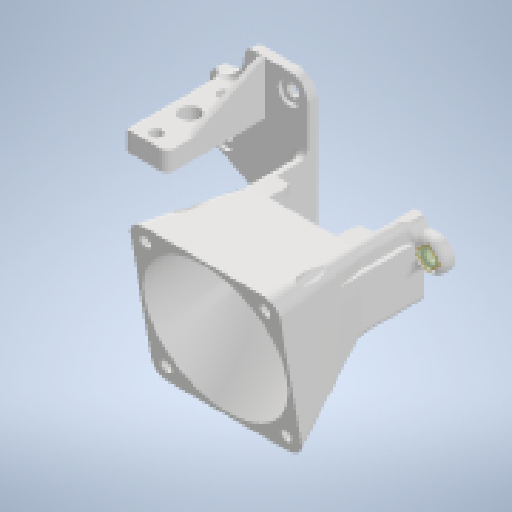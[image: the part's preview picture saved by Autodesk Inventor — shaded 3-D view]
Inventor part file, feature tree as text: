
AUTODESK INVENTOR PART (.ipt)
format: ipt  version: 2023 (Build 270158000, 158)  size: 935,936 bytes
history: native  units: mm
features: extrude x19, sketch x19, reference x19, other x11, fillet x10, plane x7, loft x2, projected_geometry x2
ambient origin geometry x8: Origin, YZ Plane, XZ Plane, XY Plane, X Axis, Y Axis, Z Axis, Center Point
bodies: Solid1 (feature_tree)
feature tree (89):
  extrude  "Extrusion1"  Depth=2.5mm TaperAngle=0.0deg
  extrude  "Extrusion2"  Depth=1.0mm TaperAngle=0.0deg
  extrude  "Extrusion3"  Depth=12.0mm TaperAngle=0.0deg
  extrude  "Extrusion4"  Depth=14.45mm TaperAngle=0.0deg
  extrude  "Extrusion6"  TaperAngle=90.0deg  [1 undecoded]
  extrude  "Extrusion7"  Depth=6.0mm
  extrude  "Extrusion8"  Depth=19.0mm
  plane  "Work Plane2"
  fillet  "Fillet1"  Radius=2.0mm
  fillet  "Fillet2"  Radius=2.0mm
  fillet  "Fillet3"  Radius=2.5mm
  extrude  "Extrusion9"  Depth=2.0mm
  fillet  "Fillet4"  Radius=38.0mm
  plane  "Work Plane4"
  sketch  "Sketch12"  dims[d38=20.0mm d40=12.217305mm]
  loft  "Loft2"
  loft  "Loft3"
  fillet  "Fillet5"  Radius=40.0mm
  extrude  "Extrusion10"  Depth=4.0mm
  fillet  "Fillet6"  Radius=2.8mm
  fillet  "Fillet7"  Radius=38.0mm
  extrude  "Extrusion11"  Depth=20.0mm
  fillet  "Fillet8"  [1 undecoded]
  extrude  "Extrusion12"  TaperAngle=0.0deg  [1 undecoded]
  plane  "Work Plane5"
  extrude  "Extrusion13"  Depth=2.0mm
  plane  "Work Plane7"
  extrude  "Extrusion16"  Depth=3.5mm
  fillet  "Fillet9"  Radius=2.5mm
  extrude  "Extrusion17"  Depth=100.0mm TaperAngle=0.0deg
  extrude  "Extrusion18"  Depth=19.5mm
  extrude  "Extrusion19"  Depth=3.0mm
  extrude  "Extrusion20"  Depth=3.75mm
  fillet  "Fillet10"  Radius=4.75mm
  extrude  "Extrusion21"  Depth=4.75mm
  plane  "Work Plane8"
  extrude  "Extrusion22"  Depth=10.0mm
  sketch  "Sketch1"  dims[d1=2.5mm d2=2.5mm d3=0.0mm]
  reference  "Reference1"
  reference  "Reference2"
  sketch  "Sketch2"  dims[d4=6.0mm d5=1.0mm d6=0.0mm]
  sketch  "Sketch3"  dims[d7=2.0mm d8=12.0mm d9=0.0mm]
  sketch  "Sketch4"  dims[d11=3.0mm d12=0.0mm d17=14.45mm d18=0.0mm]
  sketch  "Sketch6"  dims[d19=90.0deg d21=90.0deg]
  sketch  "Sketch7"  dims[d22=3.5mm d23=0.0mm d24=6.0mm]
  reference  "Reference10"
  reference  "Reference11"
  sketch  "Sketch8"  dims[d25=1.0mm d26=0.0mm d27=19.0mm d28=2.0mm d29=2.0mm d30=2.0mm d31=2.5mm]
  sketch  "Sketch9"  dims[d32=2.5mm d33=0.0mm d34=2.0mm d35=38.0mm]
  plane  "Work Plane3"
  other  "Edges2"
  other  "Edges3"
  sketch  "Sketch13"  dims[d41=80.0mm d42=90.0deg d43=40.0mm]
  sketch  "Sketch14"  dims[d44=40.0mm d45=4.0mm d46=2.8mm d49=38.0mm]
  sketch  "Sketch15"  dims[d50=20.0mm d51=20.0mm d56=0.0mm d57=90.0deg]
  plane  "Work Plane6"
  sketch  "Sketch21"  dims[d58=0.0mm d59=90.0deg d60=0.0mm d61=90.0deg d62=0.0mm d63=90.0deg]
  reference  "Reference12"
  reference  "Reference13"
  reference  "Reference14"
  reference  "Reference15"
  reference  "Reference17"
  reference  "Reference18"
  reference  "Reference19"
  sketch  "Sketch22"  dims[d67=25.0mm d68=0.0mm d69=2.0mm]
  sketch  "Sketch23"  dims[d70=2.0mm d71=3.5mm d72=2.5mm d73=0.0mm]
  sketch  "Sketch24"  dims[d74=2.0mm d75=100.0mm d76=0.0mm]
  projected_geometry  "Projected Loop1"
  projected_geometry  "Projected Loop2"
  reference  "Reference22"
  reference  "Reference23"
  reference  "Reference24"
  reference  "Reference25"
  reference  "Reference26"
  reference  "Reference27"
  reference  "Reference28"
  sketch  "Sketch25"  dims[d77=10.0mm d78=19.5mm]
  sketch  "Sketch26"  dims[d79=25.0mm d80=3.0mm]
  reference  "Reference29"
  sketch  "Sketch29"  dims[d81=1.5mm d82=3.75mm d83=4.75mm d84=4.75mm d85=10.0mm d86=5.0mm d87=0.0mm d89=90.0deg d90=20.0mm d119=5.2mm d120=12.0mm d121=26.0mm d122=0.0mm d123=2.0mm d124=3.0mm d125=18.0mm d126=5.0mm d127=9.0mm d128=1.0mm d129=26.0mm d130=0.0mm d132=5.0mm d133=5.0mm d134=5.0mm d135=23.75mm d136=0.0mm d137=2.5mm d138=0.0mm d139=1.409413mm d140=8.0mm d141=4.363323mm d142=2.5mm d143=0.0mm d144=2.0mm d145=3.0mm d146=9.0mm d147=3.5mm d148=10.0mm d149=0.0mm d152=23.058mm d153=0.0mm d107=0.5mm d108=0.872665mm d109=0.5mm d110=0.872665mm]
  other  "<userpath>\Desktop\Another3dPrinterShroud\MODELS\ENDER 3 ASSEMBLY ALTDUCT.iam"
  other  "ENDER 3 ASSEMBLY ALTDUCT.iam"
  other  "BACKPLATE:1"
  other  "ENDER 3 NOZZLE:1"
  other  "ENDER 3 E_PLATE:1"
  other  "ENDER 3 RAD:1"
  other  "<userpath> laptop\Desktop\Custom3dpFanDuct\REF_MODEL\ENDER 3 ASSEMBLY.iam"
  other  "ENDER 3 ASSEMBLY.iam"
  other  "ENDER 3 HEATBLOCK:1"
note: 3 required parameter values undecoded (feature->parameter linkage not recoverable at this tier; creation-order binding heuristic only, values carry confidence <= 0.55)
